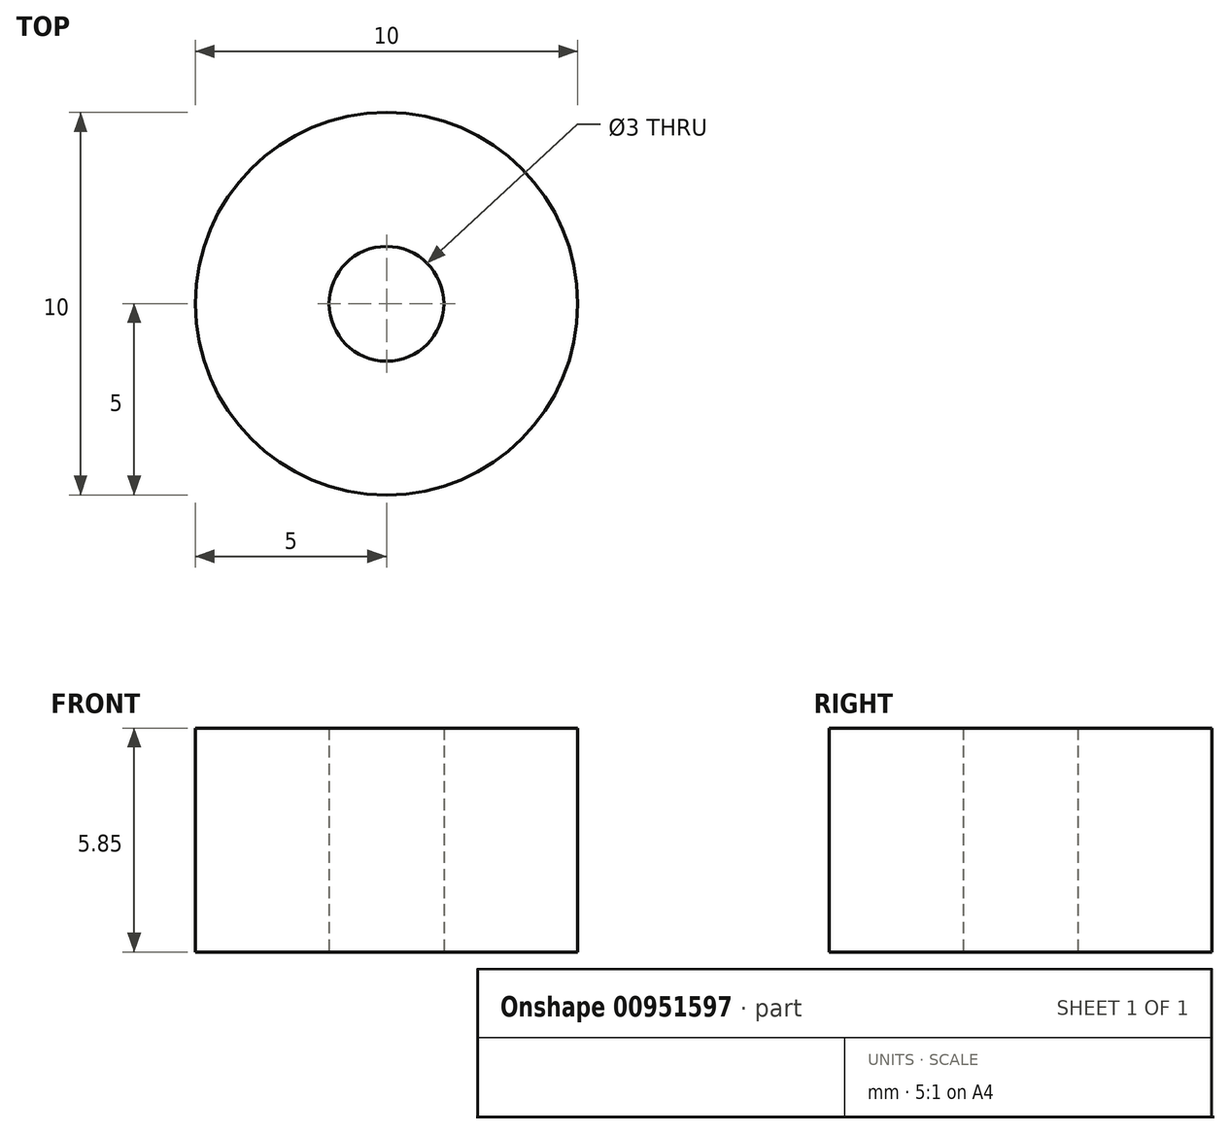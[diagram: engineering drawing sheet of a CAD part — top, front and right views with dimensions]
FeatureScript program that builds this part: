
annotation { "Feature Type Name" : "Feature", "Feature Type Description" : "" }
export const myFeature = defineFeature(function(context is Context, id is Id, definition is map)
    precondition{}
    {
        {
            var Q0;
            Q0=qCreatedBy(makeId("Top.planeOp"),FACE);
            var sketch = newSketch(context, id + "F0", { "sketchPlane" : qUnion([Q0])});
            skCircle(sketch, "E0", {"center": v(0, 0) * mm, "radius": 5 * mm});
            skCircle(sketch, "E1", {"center": v(0, 0) * mm, "radius": 1.5 * mm});
            skSolve(sketch);
        }
        {
            var Q0;
            Q0=makeQuery(id+"F0.imprint","IMPRINT",FACE,{"disambiguationData":[TD([[makeQuery(id+"F0.imprint","IMPRINT",EDGE,{"derivedFrom":sQuery(id+"F0.wireOp",EDGE,"E0")}),1.0]])]});
            extrude(context, id + "F1", {"entities" : qUnion([Q0]), "depth" : 5.85 * mm, "offsetDistance" : 25 * mm});
        }
    });
